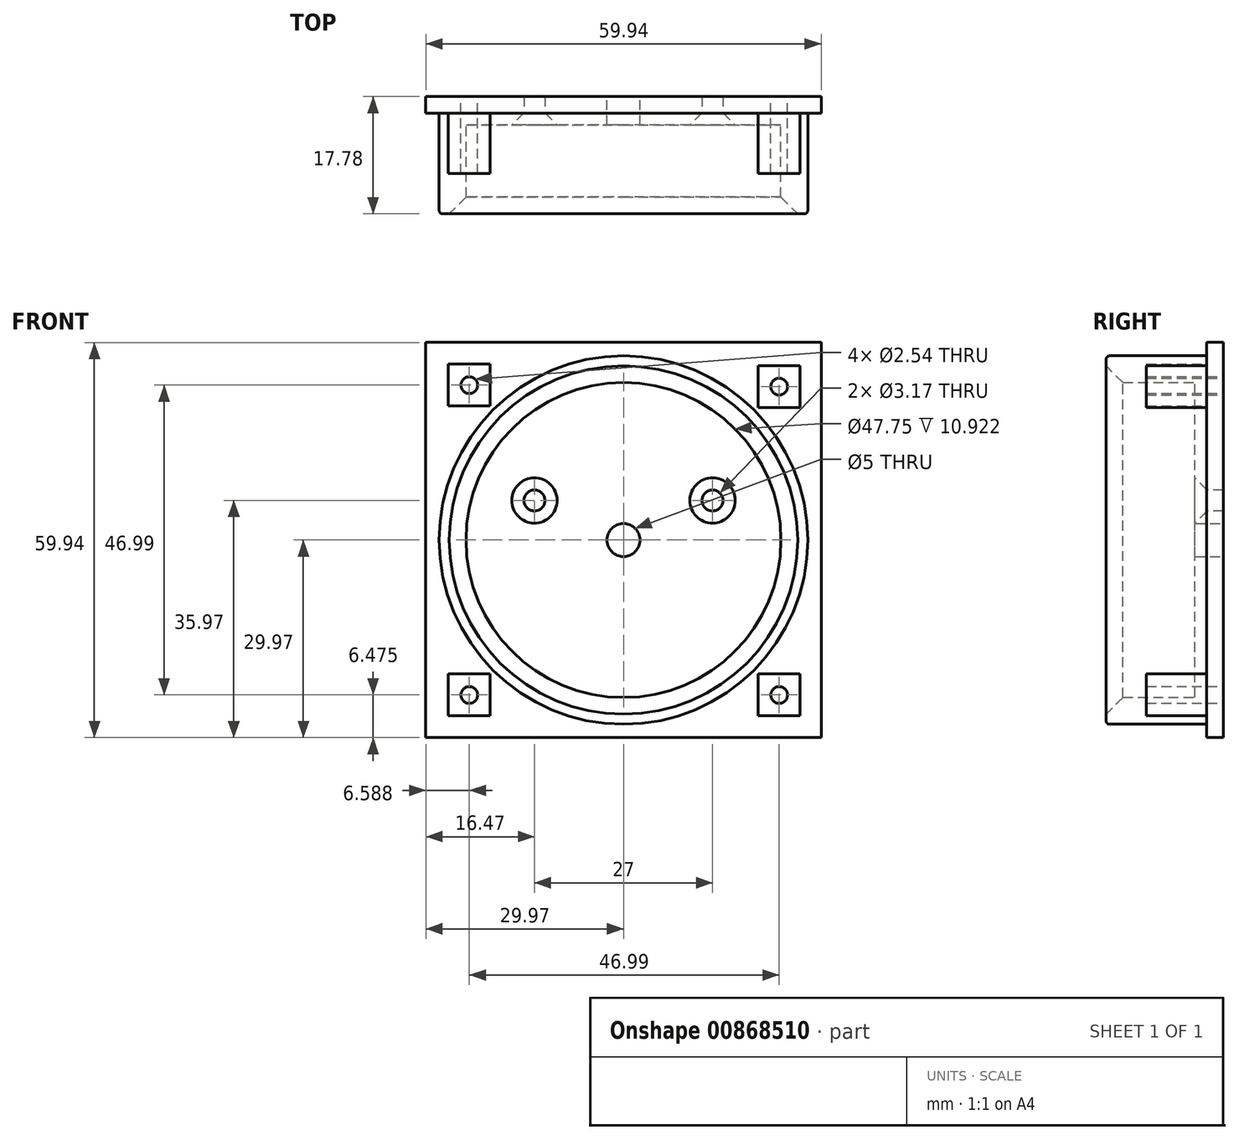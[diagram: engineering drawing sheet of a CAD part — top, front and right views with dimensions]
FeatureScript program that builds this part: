
annotation { "Feature Type Name" : "Feature", "Feature Type Description" : "" }
export const myFeature = defineFeature(function(context is Context, id is Id, definition is map)
    precondition{}
    {
        {
            var Q0;
            Q0=qCreatedBy(makeId("Front.planeOp"),FACE);
            var sketch = newSketch(context, id + "F0", { "sketchPlane" : qUnion([Q0])});
            skCircle(sketch, "E0", {"center": v(0, 0) * mm, "radius": 24.26 * mm});
            skLineSegment(sketch, "E1.bottom", {"start": v(29.97, 29.97) * mm, "end": v(-29.97, 29.97) * mm});
            skLineSegment(sketch, "E1.top", {"start": v(29.97, -29.97) * mm, "end": v(-29.97, -29.97) * mm});
            skLineSegment(sketch, "E1.left", {"start": v(29.97, 29.97) * mm, "end": v(29.97, -29.97) * mm});
            skLineSegment(sketch, "E1.right", {"start": v(-29.97, 29.97) * mm, "end": v(-29.97, -29.97) * mm});
            skPoint(sketch, "E2", {"position": v(-23.38, 23.5) * mm});
            skPoint(sketch, "E3", {"position": v(23.6, 23.27) * mm});
            skPoint(sketch, "E4", {"position": v(23.6, -23.5) * mm});
            skPoint(sketch, "E5", {"position": v(-23.38, -23.5) * mm});
            skLineSegment(sketch, "E6.bottom", {"start": v(-20.2, 26.67) * mm, "end": v(-26.56, 26.67) * mm});
            skLineSegment(sketch, "E6.top", {"start": v(-20.2, 20.32) * mm, "end": v(-26.56, 20.32) * mm});
            skLineSegment(sketch, "E6.left", {"start": v(-20.2, 26.67) * mm, "end": v(-20.2, 20.32) * mm});
            skLineSegment(sketch, "E6.right", {"start": v(-26.56, 26.67) * mm, "end": v(-26.56, 20.32) * mm});
            skLineSegment(sketch, "E7.bottom", {"start": v(26.78, 26.44) * mm, "end": v(20.43, 26.44) * mm});
            skLineSegment(sketch, "E7.top", {"start": v(26.78, 20.1) * mm, "end": v(20.43, 20.1) * mm});
            skLineSegment(sketch, "E7.left", {"start": v(26.78, 26.44) * mm, "end": v(26.78, 20.1) * mm});
            skLineSegment(sketch, "E7.right", {"start": v(20.43, 26.44) * mm, "end": v(20.43, 20.1) * mm});
            skLineSegment(sketch, "E8.bottom", {"start": v(26.78, -20.32) * mm, "end": v(20.43, -20.32) * mm});
            skLineSegment(sketch, "E8.top", {"start": v(26.78, -26.67) * mm, "end": v(20.43, -26.67) * mm});
            skLineSegment(sketch, "E8.left", {"start": v(26.78, -20.32) * mm, "end": v(26.78, -26.67) * mm});
            skLineSegment(sketch, "E8.right", {"start": v(20.43, -20.32) * mm, "end": v(20.43, -26.67) * mm});
            skLineSegment(sketch, "E9.bottom", {"start": v(-20.2, -20.32) * mm, "end": v(-26.56, -20.32) * mm});
            skLineSegment(sketch, "E9.top", {"start": v(-20.2, -26.67) * mm, "end": v(-26.56, -26.67) * mm});
            skLineSegment(sketch, "E9.left", {"start": v(-20.2, -20.32) * mm, "end": v(-20.2, -26.67) * mm});
            skLineSegment(sketch, "E9.right", {"start": v(-26.56, -20.32) * mm, "end": v(-26.56, -26.67) * mm});
            skSolve(sketch);
        }
        {
            var Q0;
            Q0=makeQuery(id+"F0.imprint","IMPRINT",FACE,{"disambiguationData":[TD([[makeQuery(id+"F0.imprint","IMPRINT",EDGE,{"derivedFrom":sQuery(id+"F0.wireOp",EDGE,"E0")}),1.0]])]});
            extrude(context, id + "F1", {"entities" : qUnion([Q0]), "depth" : 4.32 * mm, "offsetDistance" : 25.4 * mm});
        }
        {
            var Q0;
            Q0=qCreatedBy(makeId("Front.planeOp"),FACE);
            var sketch = newSketch(context, id + "F2", { "sketchPlane" : qUnion([Q0])});
            skCircle(sketch, "E10", {"center": v(0, 0) * mm, "radius": 23.88 * mm});
            skCircle(sketch, "E11", {"center": v(0, 0) * mm, "radius": 27.94 * mm});
            skSolve(sketch);
        }
        {
            var Q0;
            Q0=qSketchRegion(id+"F2",true);
            extrude(context, id + "F3", {"entities" : qUnion([Q0]), "operationType" : NewBodyOperationType.ADD, "depth" : 17.78 * mm, "offsetDistance" : 25.4 * mm});
        }
        {
            var Q0;
            Q0=qCreatedBy(makeId("Front.planeOp"),FACE);
            cPlane(context, id + "F4", {"entities" : qUnion([Q0]), "cplaneType" : CPlaneType.OFFSET, "offset" : 2.54 * mm, "width" : 152.4 * mm, "height" : 152.4 * mm});
        }
        {
            var Q0;
            Q0=makeQuery(id+"F0.imprint","IMPRINT",FACE,{"disambiguationData":[TD([[makeQuery(id+"F0.imprint","IMPRINT",EDGE,{"derivedFrom":sQuery(id+"F0.wireOp",EDGE,"E0")}),-1.0]])]});
            extrude(context, id + "F5", {"entities" : qUnion([Q0]), "operationType" : NewBodyOperationType.ADD, "depth" : 2.54 * mm, "offsetDistance" : 25.4 * mm});
        }
        {
            var Q0;
            Q0=makeQuery(id+"F0.imprint","IMPRINT",FACE,{"disambiguationData":[TD([[makeQuery(id+"F0.imprint","IMPRINT",EDGE,{"derivedFrom":sQuery(id+"F0.wireOp",EDGE,"E9.bottom")}),1.0]])]});
            var Q1;
            Q1=makeQuery(id+"F0.imprint","IMPRINT",FACE,{"disambiguationData":[TD([[makeQuery(id+"F0.imprint","IMPRINT",EDGE,{"derivedFrom":sQuery(id+"F0.wireOp",EDGE,"E6.bottom")}),1.0]])]});
            var Q2;
            Q2=makeQuery(id+"F0.imprint","IMPRINT",FACE,{"disambiguationData":[TD([[makeQuery(id+"F0.imprint","IMPRINT",EDGE,{"derivedFrom":sQuery(id+"F0.wireOp",EDGE,"E7.bottom")}),1.0]])]});
            var Q3;
            Q3=makeQuery(id+"F0.imprint","IMPRINT",FACE,{"disambiguationData":[TD([[makeQuery(id+"F0.imprint","IMPRINT",EDGE,{"derivedFrom":sQuery(id+"F0.wireOp",EDGE,"E8.bottom")}),1.0]])]});
            extrude(context, id + "F6", {"entities" : qUnion([Q0, Q1, Q2, Q3]), "operationType" : NewBodyOperationType.ADD, "depth" : 11.68 * mm, "offsetDistance" : 25.4 * mm});
        }
        {
            var Q0;
            Q0=sQuery(id+"F0.wireOp",VERTEX,"E2");
            var Q1;
            Q1=sQuery(id+"F0.wireOp",VERTEX,"E3");
            var Q2;
            Q2=sQuery(id+"F0.wireOp",VERTEX,"E5");
            var Q3;
            Q3=sQuery(id+"F0.wireOp",VERTEX,"E4");
            var Q4;
            Q4=makeQuery(id+"F1.opExtrude","SWEPT_BODY",BODY,{"disambiguationData":[OSD([sQuery(id+"F0.wireOp",EDGE,"E0"),sQuery(id+"F0.wireOp",EDGE,"mUU7OhdX-XNa0-4Drs-y0eB-kvNcseM0QuPt"),sQuery(id+"F0.wireOp",EDGE,"VLppaxhi-9gsj-CoUi-4eyW-4ZfSdwgNkN1v"),sQuery(id+"F0.wireOp",EDGE,"52aOqeBn-3A06-FGgB-2pqV-L4Iadewni0vA"),sQuery(id+"F0.wireOp",EDGE,"DvhnZx25-jBlL-CNyz-VQNl-D04Q6eJg0ANY.bottom"),sQuery(id+"F0.wireOp",EDGE,"DvhnZx25-jBlL-CNyz-VQNl-D04Q6eJg0ANY.top")])]});
            hole(context, id + "F7", {"style" : HoleStyle.SIMPLE, "endStyle" : HoleEndStyle.THROUGH, "oppositeDirection" : true, "holeDiameter" : 2.54 * mm, "majorDiameter" : 6.35 * mm, "isTappedThrough" : true, "tappedDepth" : 12.7 * mm, "tapClearance" : 3, "locations" : qUnion([Q0, Q1, Q2, Q3]), "scope" : qUnion([Q4])});
        }
        {
            var Q0;
            Q0=makeQuery(id+"F3.opExtrude","CAP_EDGE",EDGE,{"disambiguationData":[OSD([sQuery(id+"F2.wireOp",EDGE,"E10")])],"isStart":false});
            chamfer(context, id + "F8", {"entities" : qUnion([Q0]), "width" : 2.54 * mm, "tangentPropagation" : true});
        }
        {
            var Q0;
            Q0=makeQuery(id+"F3.opExtrude","CAP_EDGE",EDGE,{"disambiguationData":[OSD([sQuery(id+"F2.wireOp",EDGE,"E11")])],"isStart":false});
            fillet(context, id + "F9", {"entities" : qUnion([Q0]), "radius" : 0.5 * mm, "tangentPropagation" : true, "allowEdgeOverflow" : false});
        }
        {
            var Q0;
            Q0=makeQuery(id+"F1.opExtrude","CAP_FACE",FACE,{"disambiguationData":[OSD([sQuery(id+"F0.wireOp",EDGE,"E0")])],"isStart":false});
            var sketch = newSketch(context, id + "F10", { "sketchPlane" : qUnion([Q0])});
            skPoint(sketch, "E12", {"position": v(-13.5, 6) * mm});
            skPoint(sketch, "E13", {"position": v(13.5, 6) * mm});
            skSolve(sketch);
        }
        {
            var Q0;
            Q0=sQuery(id+"F10.wireOp",VERTEX,"E12");
            var Q1;
            Q1=sQuery(id+"F10.wireOp",VERTEX,"E13");
            var Q2;
            Q2=makeQuery(id+"F1.opExtrude","SWEPT_BODY",BODY,{"disambiguationData":[OSD([sQuery(id+"F0.wireOp",EDGE,"E0")])]});
            hole(context, id + "F11", {"style" : HoleStyle.C_SINK, "endStyle" : HoleEndStyle.THROUGH, "holeDiameter" : 3.17 * mm, "cSinkDiameter" : 6.86 * mm, "cSinkAngle" : 90 * degree, "majorDiameter" : 6.35 * mm, "isTappedThrough" : true, "tappedDepth" : 12.7 * mm, "tapClearance" : 3, "locations" : qUnion([Q0, Q1]), "scope" : qUnion([Q2])});
        }
        {
            var Q0;
            Q0=sQuery(id+"F0.wireOp",VERTEX,"E0.center");
            var Q1;
            Q1=makeQuery(id+"F1.opExtrude","SWEPT_BODY",BODY,{"disambiguationData":[OSD([sQuery(id+"F0.wireOp",EDGE,"E0")])]});
            hole(context, id + "F12", {"style" : HoleStyle.SIMPLE, "endStyle" : HoleEndStyle.THROUGH, "oppositeDirection" : true, "holeDiameter" : 5 * mm, "majorDiameter" : 6.35 * mm, "isTappedThrough" : true, "tappedDepth" : 12.7 * mm, "tapClearance" : 3, "locations" : qUnion([Q0]), "scope" : qUnion([Q1])});
        }
    });
